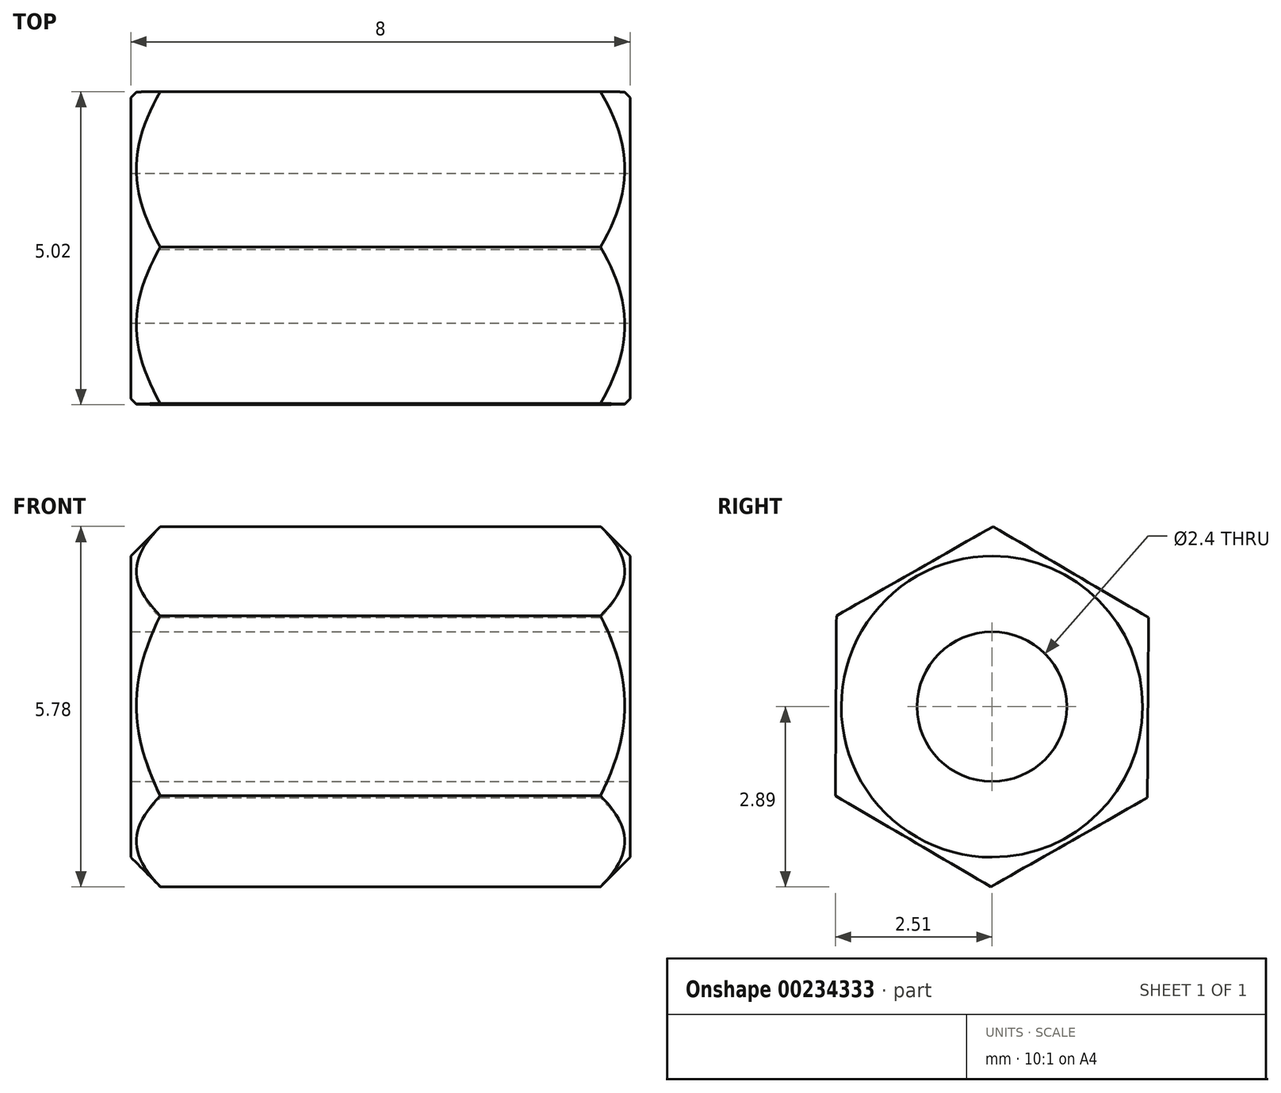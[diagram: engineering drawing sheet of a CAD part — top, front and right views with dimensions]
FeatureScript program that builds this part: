
annotation { "Feature Type Name" : "Feature", "Feature Type Description" : "" }
export const myFeature = defineFeature(function(context is Context, id is Id, definition is map)
    precondition{}
    {
        {
            var Q0;
            Q0=qCreatedBy(makeId("Right.planeOp"),FACE);
            var sketch = newSketch(context, id + "F0", { "sketchPlane" : qUnion([Q0])});
            skCircle(sketch, "E0.cCircle", {"center": v(0, 0) * mm, "radius": 2.5 * mm, "construction": true});
            skLineSegment(sketch, "E0.0", {"start": v(2.5, -1.46) * mm, "end": v(-0.02, -2.89) * mm});
            skLineSegment(sketch, "E0.1", {"start": v(-0.02, -2.89) * mm, "end": v(-2.5, -1.43) * mm});
            skLineSegment(sketch, "E0.2", {"start": v(-2.5, -1.43) * mm, "end": v(-2.5, 1.46) * mm});
            skLineSegment(sketch, "E0.3", {"start": v(-2.5, 1.46) * mm, "end": v(0.02, 2.89) * mm});
            skLineSegment(sketch, "E0.4", {"start": v(0.02, 2.89) * mm, "end": v(2.5, 1.43) * mm});
            skLineSegment(sketch, "E0.5", {"start": v(2.5, 1.43) * mm, "end": v(2.5, -1.46) * mm});
            skPoint(sketch, "E0.0.midPoint", {"position": v(1.24, -2.17) * mm});
            skCircle(sketch, "E1", {"center": v(0, 0) * mm, "radius": 1.2 * mm});
            skSolve(sketch);
        }
        {
            var Q0;
            Q0=makeQuery(id+"F0.imprint","IMPRINT",FACE,{"disambiguationData":[TD([[makeQuery(id+"F0.imprint","IMPRINT",EDGE,{"derivedFrom":sQuery(id+"F0.wireOp",EDGE,"E0.0")}),-1.0]])]});
            extrude(context, id + "F1", {"entities" : qUnion([Q0]), "oppositeDirection" : true, "depth" : 8 * mm, "symmetric" : true});
        }
        {
            var Q0;
            Q0=qCreatedBy(makeId("Front.planeOp"),FACE);
            var sketch = newSketch(context, id + "F2", { "sketchPlane" : qUnion([Q0])});
            skLineSegment(sketch, "E2", {"start": v(4.74, -1.68) * mm, "end": v(4.74, -3.68) * mm});
            skLineSegment(sketch, "E3", {"start": v(4.74, -3.68) * mm, "end": v(2.74, -3.68) * mm});
            skLineSegment(sketch, "E4", {"start": v(2.74, -3.68) * mm, "end": v(4.74, -1.68) * mm});
            skLineSegment(sketch, "E5", {"start": v(9.88, 0) * mm, "end": v(-9.88, 0) * mm});
            skLineSegment(sketch, "E6", {"start": v(0, 0) * mm, "end": v(0, -4.96) * mm, "construction": true});
            skPoint(sketch, "E6.endSnap0", {"position": v(0, 0) * mm});
            skLineSegment(sketch, "E7.MirrorCS", {"start": v(-4.74, -3.68) * mm, "end": v(-2.74, -3.68) * mm});
            skLineSegment(sketch, "E8.MirrorCS", {"start": v(-4.74, -1.68) * mm, "end": v(-4.74, -3.68) * mm});
            skLineSegment(sketch, "E9.MirrorCS", {"start": v(-2.74, -3.68) * mm, "end": v(-4.74, -1.68) * mm});
            skSolve(sketch);
        }
        {
            var Q0;
            Q0=makeQuery(id+"F2.imprint","IMPRINT",FACE,{"disambiguationData":[TD([[makeQuery(id+"F2.imprint","IMPRINT",EDGE,{"derivedFrom":sQuery(id+"F2.wireOp",EDGE,"E2")}),-1.0]])]});
            var Q1;
            Q1=makeQuery(id+"F2.imprint","IMPRINT",FACE,{"disambiguationData":[TD([[makeQuery(id+"F2.imprint","IMPRINT",EDGE,{"derivedFrom":sQuery(id+"F2.wireOp",EDGE,"E7.MirrorCS")}),1.0]])]});
            var Q2;
            Q2=sQuery(id+"F2.wireOp",EDGE,"E4");
            var Q3;
            Q3=sQuery(id+"F2.wireOp",EDGE,"E5");
            revolve(context, id + "F3", {"operationType" : NewBodyOperationType.REMOVE, "entities" : qUnion([Q0, Q1]), "surfaceEntities" : qUnion([Q2]), "axis" : qUnion([Q3]), "revolveType" : RevolveType.FULL, "oppositeDirection" : true});
        }
    });
